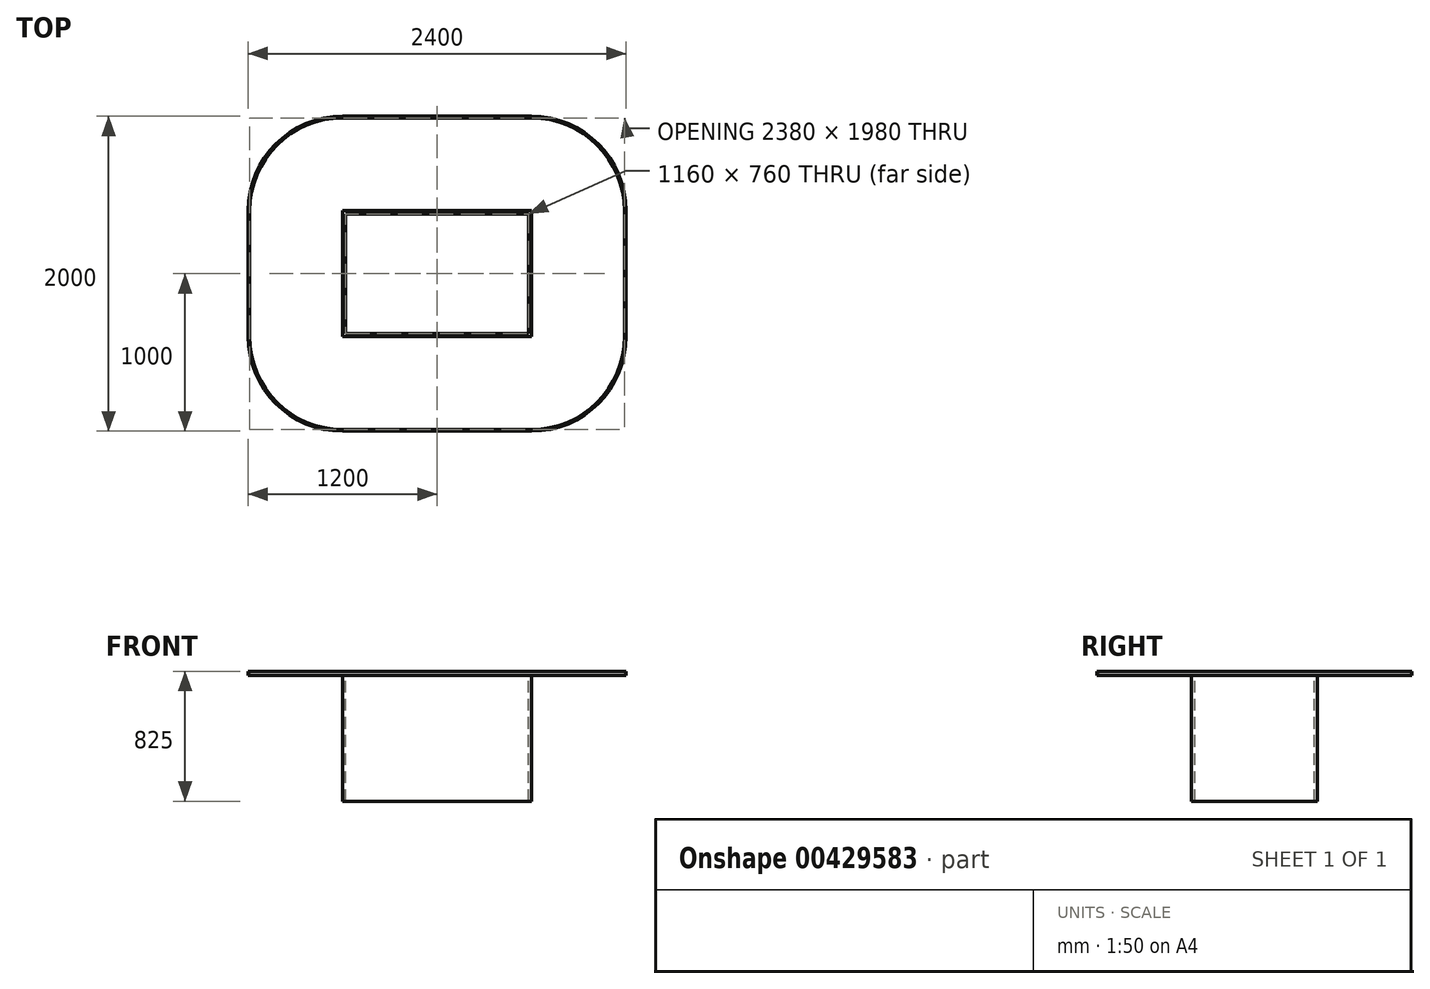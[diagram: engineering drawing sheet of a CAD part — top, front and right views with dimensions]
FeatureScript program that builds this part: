
annotation { "Feature Type Name" : "Feature", "Feature Type Description" : "" }
export const myFeature = defineFeature(function(context is Context, id is Id, definition is map)
    precondition{}
    {
        {
            var Q0;
            Q0=qCreatedBy(makeId("Top.planeOp"),FACE);
            var sketch = newSketch(context, id + "F0", { "sketchPlane" : qUnion([Q0])});
            skLineSegment(sketch, "E0.bottom", {"start": v(-600, 400) * mm, "end": v(600, 400) * mm});
            skLineSegment(sketch, "E0.top", {"start": v(-600, -400) * mm, "end": v(600, -400) * mm});
            skLineSegment(sketch, "E0.left", {"start": v(-600, 400) * mm, "end": v(-600, -400) * mm});
            skLineSegment(sketch, "E0.right", {"start": v(600, 400) * mm, "end": v(600, -400) * mm});
            skLineSegment(sketch, "E1", {"start": v(0, -1000) * mm, "end": v(0, -400) * mm, "construction": true});
            skLineSegment(sketch, "E2", {"start": v(600, 0) * mm, "end": v(1200, 0) * mm, "construction": true});
            skPoint(sketch, "E2.endSnap0", {"position": v(-600, 0) * mm});
            skLineSegment(sketch, "E3", {"start": v(-600, -1000) * mm, "end": v(-600, 1000) * mm, "construction": true});
            skLineSegment(sketch, "E4", {"start": v(600, -1000) * mm, "end": v(600, 1000) * mm, "construction": true});
            skLineSegment(sketch, "E5", {"start": v(1200, 1000) * mm, "end": v(-1200, 1000) * mm, "construction": true});
            skLineSegment(sketch, "E6", {"start": v(-1200, 1000) * mm, "end": v(-1200, -1000) * mm, "construction": true});
            skLineSegment(sketch, "E7", {"start": v(-1200, -1000) * mm, "end": v(1200, -1000) * mm, "construction": true});
            skLineSegment(sketch, "E8", {"start": v(1200, -1000) * mm, "end": v(1200, 1000) * mm, "construction": true});
            skLineSegment(sketch, "E9", {"start": v(-1200, 400) * mm, "end": v(1200, 400) * mm, "construction": true});
            skLineSegment(sketch, "E10", {"start": v(1200, 400) * mm, "end": v(1200, -400) * mm, "construction": true});
            skLineSegment(sketch, "E11", {"start": v(1200, -400) * mm, "end": v(-1200, -400) * mm, "construction": true});
            skLineSegment(sketch, "E12.trimOffspring", {"start": v(0, 400) * mm, "end": v(0, 1000) * mm, "construction": true});
            skLineSegment(sketch, "E13", {"start": v(-600, 0) * mm, "end": v(-1200, 0) * mm, "construction": true});
            skLineSegment(sketch, "E14", {"start": v(-600, 1000) * mm, "end": v(600, 1000) * mm});
            skLineSegment(sketch, "E15", {"start": v(1200, 400) * mm, "end": v(1200, -400) * mm});
            skLineSegment(sketch, "E16", {"start": v(600, -1000) * mm, "end": v(-600, -1000) * mm});
            skLineSegment(sketch, "E17", {"start": v(-1200, -400) * mm, "end": v(-1200, 400) * mm});
            skSolve(sketch);
        }
        {
            var Q0;
            Q0=makeQuery(id+"F0.imprint","IMPRINT",FACE,{"disambiguationData":[TD([[makeQuery(id+"F0.imprint","IMPRINT",EDGE,{"derivedFrom":sQuery(id+"F0.wireOp",EDGE,"E0.bottom")}),-1.0]])]});
            var sketch = newSketch(context, id + "F1", { "sketchPlane" : qUnion([Q0])});
            skLineSegment(sketch, "E18.bottom", {"start": v(600, -400) * mm, "end": v(-600, -400) * mm});
            skLineSegment(sketch, "E18.top", {"start": v(600, 400) * mm, "end": v(-600, 400) * mm});
            skLineSegment(sketch, "E18.left", {"start": v(600, -400) * mm, "end": v(600, 400) * mm});
            skLineSegment(sketch, "E18.right", {"start": v(-600, -400) * mm, "end": v(-600, 400) * mm});
            skSolve(sketch);
        }
        {
            var Q0;
            Q0 = qSketchRegion(id + "F1", true);
            var Q1;
            Q1=sQuery(id+"F1.wireOp",EDGE,"E18.right");
            var Q2;
            Q2=sQuery(id+"F1.wireOp",EDGE,"E18.top");
            var Q3;
            Q3=sQuery(id+"F1.wireOp",EDGE,"E18.left");
            var Q4;
            Q4=sQuery(id+"F1.wireOp",EDGE,"E18.bottom");
            extrude(context, id + "F2", {"entities" : qUnion([Q0]), "surfaceEntities" : qUnion([Q1, Q2, Q3, Q4]), "oppositeDirection" : true, "depth" : 800 * mm});
        }
        {
            var Q0;
            Q0=makeQuery(id+"F0.imprint","IMPRINT",FACE,{"disambiguationData":[TD([[makeQuery(id+"F0.imprint","IMPRINT",EDGE,{"derivedFrom":sQuery(id+"F0.wireOp",EDGE,"E0.bottom")}),-1.0]])]});
            var sketch = newSketch(context, id + "F3", { "sketchPlane" : qUnion([Q0])});
            skLineSegment(sketch, "E19", {"start": v(-600, 1000) * mm, "end": v(600, 1000) * mm});
            skLineSegment(sketch, "E20", {"start": v(-1200, 400) * mm, "end": v(-1200, -400) * mm});
            skArc(sketch, "E21", {"start": v(-1200, 400) * mm, "mid": v(-1024.26, 824.26) * mm, "end": v(-600, 1000) * mm});
            skArc(sketch, "E22.MirrorCS", {"start": v(1200, 400) * mm, "mid": v(1024.26, 824.26) * mm, "end": v(600, 1000) * mm});
            skLineSegment(sketch, "E23.MirrorCS", {"start": v(1200, 400) * mm, "end": v(1200, -400) * mm});
            skArc(sketch, "E24.MirrorCS", {"start": v(1200, -400) * mm, "mid": v(1024.26, -824.26) * mm, "end": v(600, -1000) * mm});
            skLineSegment(sketch, "E25.MirrorCS", {"start": v(-600, -1000) * mm, "end": v(600, -1000) * mm});
            skArc(sketch, "E26.MirrorCS", {"start": v(-1200, -400) * mm, "mid": v(-1024.26, -824.26) * mm, "end": v(-600, -1000) * mm});
            skLineSegment(sketch, "E27.0", {"start": v(-600, 400) * mm, "end": v(600, 400) * mm});
            skLineSegment(sketch, "E28.0", {"start": v(600, 400) * mm, "end": v(600, -400) * mm});
            skLineSegment(sketch, "E29.0", {"start": v(-600, -400) * mm, "end": v(600, -400) * mm});
            skLineSegment(sketch, "E30.0", {"start": v(-600, 400) * mm, "end": v(-600, -400) * mm});
            skArc(sketch, "E31.0", {"start": v(-1190, -400) * mm, "mid": v(-1017.2, -817.2) * mm, "end": v(-600, -990) * mm});
            skLineSegment(sketch, "E31.1", {"start": v(-1190, 400) * mm, "end": v(-1190, -400) * mm});
            skLineSegment(sketch, "E31.2", {"start": v(-600, -990) * mm, "end": v(600, -990) * mm});
            skArc(sketch, "E31.3", {"start": v(-1190, 400) * mm, "mid": v(-1017.2, 817.2) * mm, "end": v(-600, 990) * mm});
            skArc(sketch, "E31.4", {"start": v(1190, -400) * mm, "mid": v(1017.2, -817.2) * mm, "end": v(600, -990) * mm});
            skLineSegment(sketch, "E31.5", {"start": v(1190, 400) * mm, "end": v(1190, -400) * mm});
            skArc(sketch, "E31.6", {"start": v(1190, 400) * mm, "mid": v(1017.2, 817.2) * mm, "end": v(600, 990) * mm});
            skLineSegment(sketch, "E31.7", {"start": v(-600, 990) * mm, "end": v(600, 990) * mm});
            skSolve(sketch);
        }
        {
            var Q0;
            Q0 = qSketchRegion(id + "F3", true);
            extrude(context, id + "F4", {"entities" : qUnion([Q0]), "operationType" : NewBodyOperationType.ADD, "depth" : 25 * mm});
        }
        {
            var Q0;
            Q0=makeQuery(id+"F2.opExtrude","CAP_FACE",FACE,{"disambiguationData":[OSD([sQuery(id+"F1.wireOp",EDGE,"E18.bottom"),sQuery(id+"F1.wireOp",EDGE,"E18.top"),sQuery(id+"F1.wireOp",EDGE,"E18.left"),sQuery(id+"F1.wireOp",EDGE,"E18.right")])],"isStart":true});
            var Q1;
            Q1=makeQuery(id+"F2.opExtrude","CAP_FACE",FACE,{"disambiguationData":[OSD([sQuery(id+"F1.wireOp",EDGE,"E18.bottom"),sQuery(id+"F1.wireOp",EDGE,"E18.top"),sQuery(id+"F1.wireOp",EDGE,"E18.left"),sQuery(id+"F1.wireOp",EDGE,"E18.right")])],"isStart":false});
            shell(context, id + "F5", {"entities" : qUnion([Q0, Q1]), "thickness" : 20 * mm});
        }
    });
